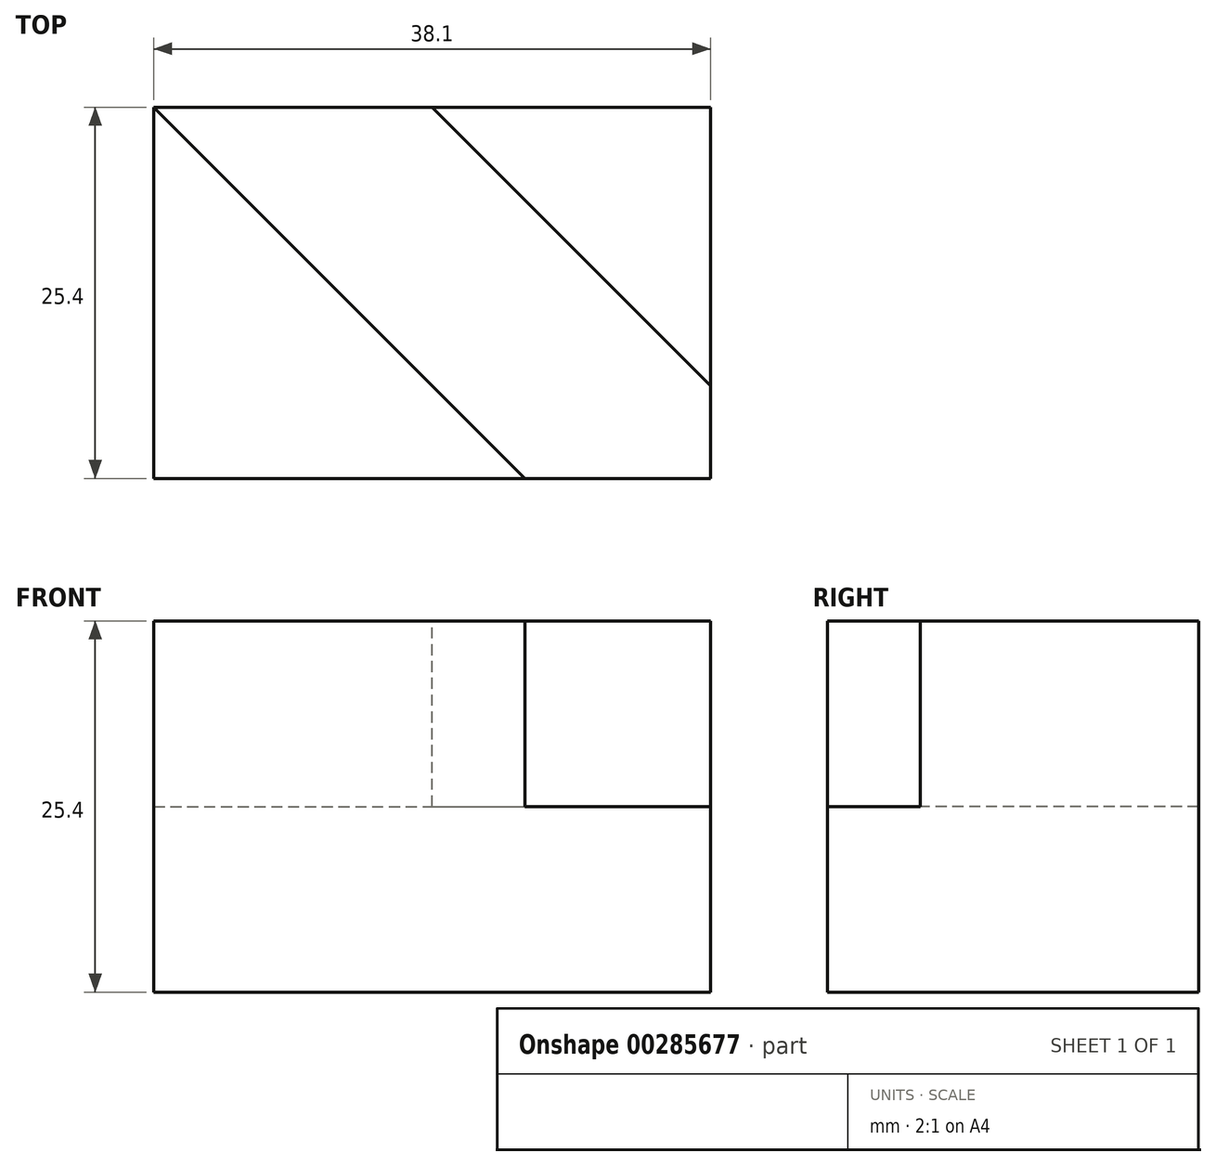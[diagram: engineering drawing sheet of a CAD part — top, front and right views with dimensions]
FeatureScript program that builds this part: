
annotation { "Feature Type Name" : "Feature", "Feature Type Description" : "" }
export const myFeature = defineFeature(function(context is Context, id is Id, definition is map)
    precondition{}
    {
        {
            var Q0;
            Q0=qCreatedBy(makeId("Front.planeOp"),FACE);
            var sketch = newSketch(context, id + "F0", { "sketchPlane" : qUnion([Q0])});
            skLineSegment(sketch, "E0", {"start": v(0, 0) * mm, "end": v(0, 25.4) * mm});
            skLineSegment(sketch, "E1", {"start": v(0, 25.4) * mm, "end": v(38.1, 25.4) * mm});
            skLineSegment(sketch, "E2", {"start": v(38.1, 25.4) * mm, "end": v(38.1, 0) * mm});
            skLineSegment(sketch, "E3", {"start": v(38.1, 0) * mm, "end": v(0, 0) * mm});
            skSolve(sketch);
        }
        {
            var Q0;
            Q0=makeQuery(id+"F0.imprint","IMPRINT",FACE,{"disambiguationData":[TD([[makeQuery(id+"F0.imprint","IMPRINT",EDGE,{"derivedFrom":sQuery(id+"F0.wireOp",EDGE,"E0")}),-1.0]])]});
            extrude(context, id + "F1", {"entities" : qUnion([Q0]), "depth" : 25.4 * mm});
        }
        {
            var Q0;
            Q0=makeQuery(id+"F1.opExtrude","SWEPT_FACE",FACE,{"disambiguationData":[OSD([sQuery(id+"F0.wireOp",EDGE,"E1")])]});
            var sketch = newSketch(context, id + "F2", { "sketchPlane" : qUnion([Q0])});
            skLineSegment(sketch, "E4", {"start": v(0, 0) * mm, "end": v(25.4, -25.4) * mm});
            skLineSegment(sketch, "E5", {"start": v(19.05, 0) * mm, "end": v(38.1, -19.05) * mm});
            skLineSegment(sketch, "E6", {"start": v(0, 0) * mm, "end": v(19.05, 0) * mm});
            skLineSegment(sketch, "E7", {"start": v(25.4, -25.4) * mm, "end": v(38.1, -25.4) * mm});
            skLineSegment(sketch, "E8", {"start": v(38.1, -25.4) * mm, "end": v(38.1, -19.05) * mm});
            skSolve(sketch);
        }
        {
            var Q0;
            Q0=makeQuery(id+"F2.imprint","IMPRINT",FACE,{"disambiguationData":[TD([[makeQuery(id+"F2.imprint","IMPRINT",EDGE,{"derivedFrom":sQuery(id+"F2.wireOp",EDGE,"E4")}),1.0]])]});
            extrude(context, id + "F3", {"entities" : qUnion([Q0]), "operationType" : NewBodyOperationType.REMOVE, "oppositeDirection" : true, "depth" : 12.7 * mm});
        }
    });
